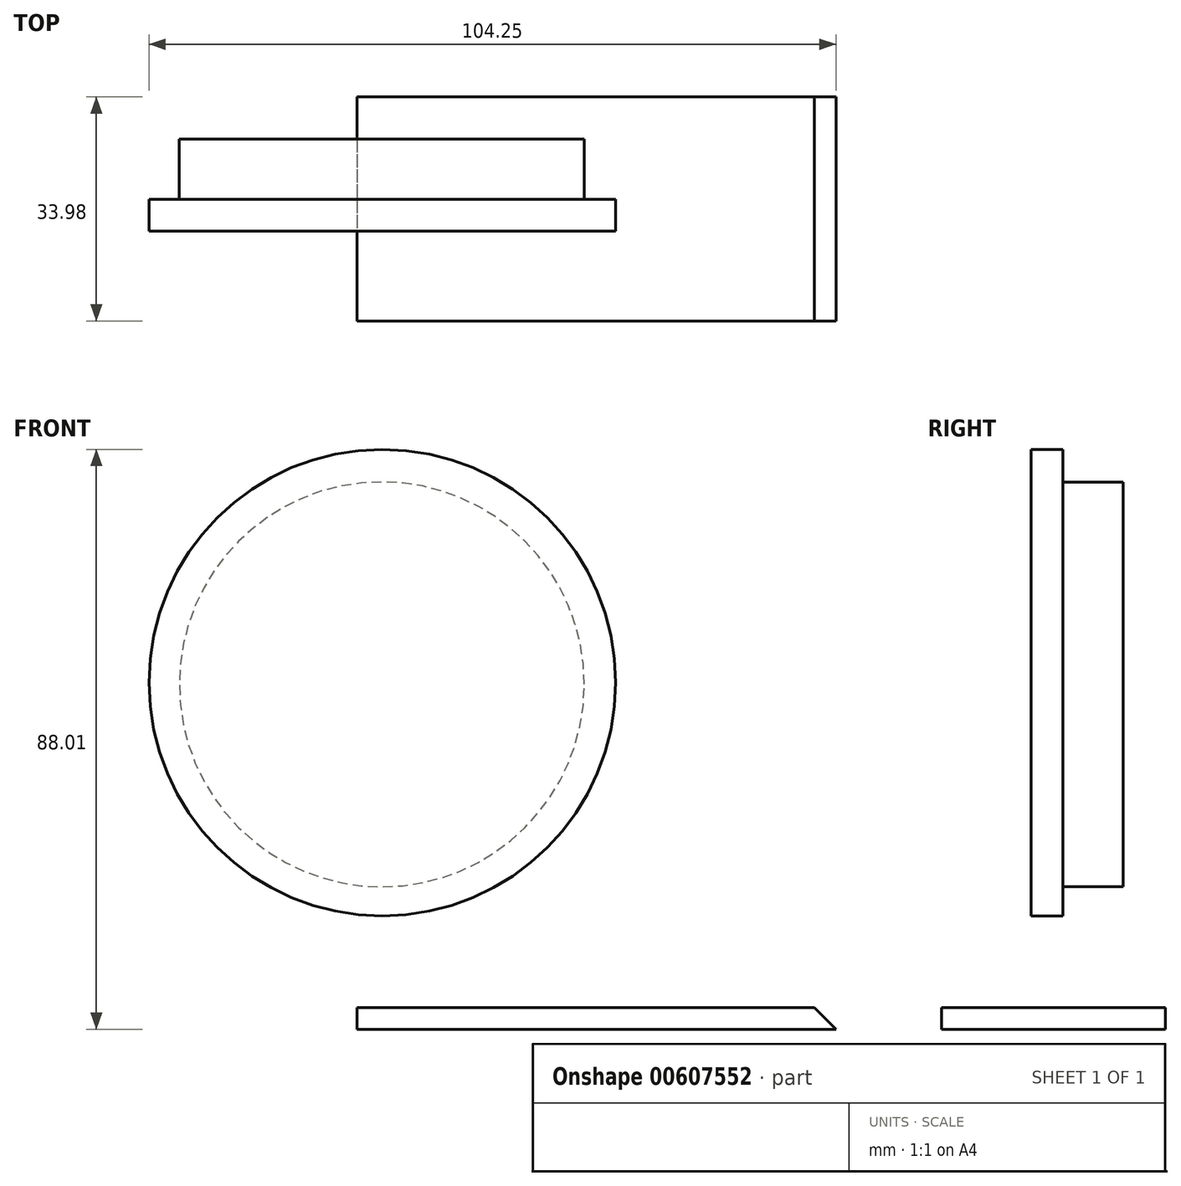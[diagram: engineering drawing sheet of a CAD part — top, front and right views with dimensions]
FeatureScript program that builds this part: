
annotation { "Feature Type Name" : "Feature", "Feature Type Description" : "" }
export const myFeature = defineFeature(function(context is Context, id is Id, definition is map)
    precondition{}
    {
        {
            var Q0;
            Q0=qCreatedBy(makeId("Top.planeOp"),FACE);
            var sketch = newSketch(context, id + "F0", { "sketchPlane" : qUnion([Q0])});
            skLineSegment(sketch, "E0.bottom", {"start": v(-35.98, 15.51) * mm, "end": v(38.5, 15.51) * mm});
            skLineSegment(sketch, "E0.top", {"start": v(-35.98, -18.47) * mm, "end": v(38.5, -18.47) * mm});
            skLineSegment(sketch, "E0.left", {"start": v(-35.98, 15.51) * mm, "end": v(-35.98, -18.47) * mm});
            skLineSegment(sketch, "E0.right", {"start": v(38.5, 15.51) * mm, "end": v(38.5, -18.47) * mm});
            skSolve(sketch);
        }
        {
            var Q0;
            Q0 = qSketchRegion(id + "F0", true);
            extrude(context, id + "F1", {"entities" : qUnion([Q0]), "depth" : 3.3 * mm, "offsetDistance" : 25.4 * mm});
        }
        {
            var Q0;
            Q0=qCreatedBy(makeId("Front.planeOp"),FACE);
            var sketch = newSketch(context, id + "F2", { "sketchPlane" : qUnion([Q0])});
            skCircle(sketch, "E1", {"center": v(-32.14, 52.6) * mm, "radius": 35.4 * mm});
            skSolve(sketch);
        }
        {
            var Q0;
            Q0 = qSketchRegion(id + "F2", true);
            var Q1;
            Q1=makeQuery(id+"F2.imprint","IMPRINT",FACE,{"disambiguationData":[TD([[makeQuery(id+"F2.imprint","IMPRINT",EDGE,{"derivedFrom":sQuery(id+"F2.wireOp",EDGE,"E1")}),1.0]])]});
            extrude(context, id + "F3", {"entities" : qUnion([Q0, Q1]), "depth" : 4.83 * mm, "offsetDistance" : 25.4 * mm});
        }
        {
            var Q0;
            Q0=makeQuery(id+"F1.opExtrude","CAP_EDGE",EDGE,{"disambiguationData":[OSD([sQuery(id+"F0.wireOp",EDGE,"E0.right")])],"isStart":false});
            chamfer(context, id + "F4", {"entities" : qUnion([Q0]), "width" : 5.08 * mm, "tangentPropagation" : true});
        }
        {
            var Q0;
            Q0=qCreatedBy(makeId("Front.planeOp"),FACE);
            var sketch = newSketch(context, id + "F5", { "sketchPlane" : qUnion([Q0])});
            skCircle(sketch, "E2", {"center": v(-54.05, 78.5) * mm, "radius": 30.72 * mm});
            skSolve(sketch);
        }
        {
            var Q0;
            Q0 = qSketchRegion(id + "F5", true);
            extrude(context, id + "F6", {"entities" : qUnion([Q0]), "oppositeDirection" : true, "depth" : 9.14 * mm, "offsetDistance" : 25.4 * mm});
        }
        {
            var Q0;
            Q0=makeQuery(id+"F6.opExtrude","SWEPT_BODY",BODY,{"disambiguationData":[OSD([sQuery(id+"F5.wireOp",EDGE,"E2")])]});
            transform(context, id + "F7", {"entities" : qUnion([Q0]), "transformType" : TransformType.TRANSLATION_3D, "dx" : 21.84 * mm, "dy" : 0 * mm, "dz" : -26.16 * mm, "makeCopy" : false});
        }
    });
